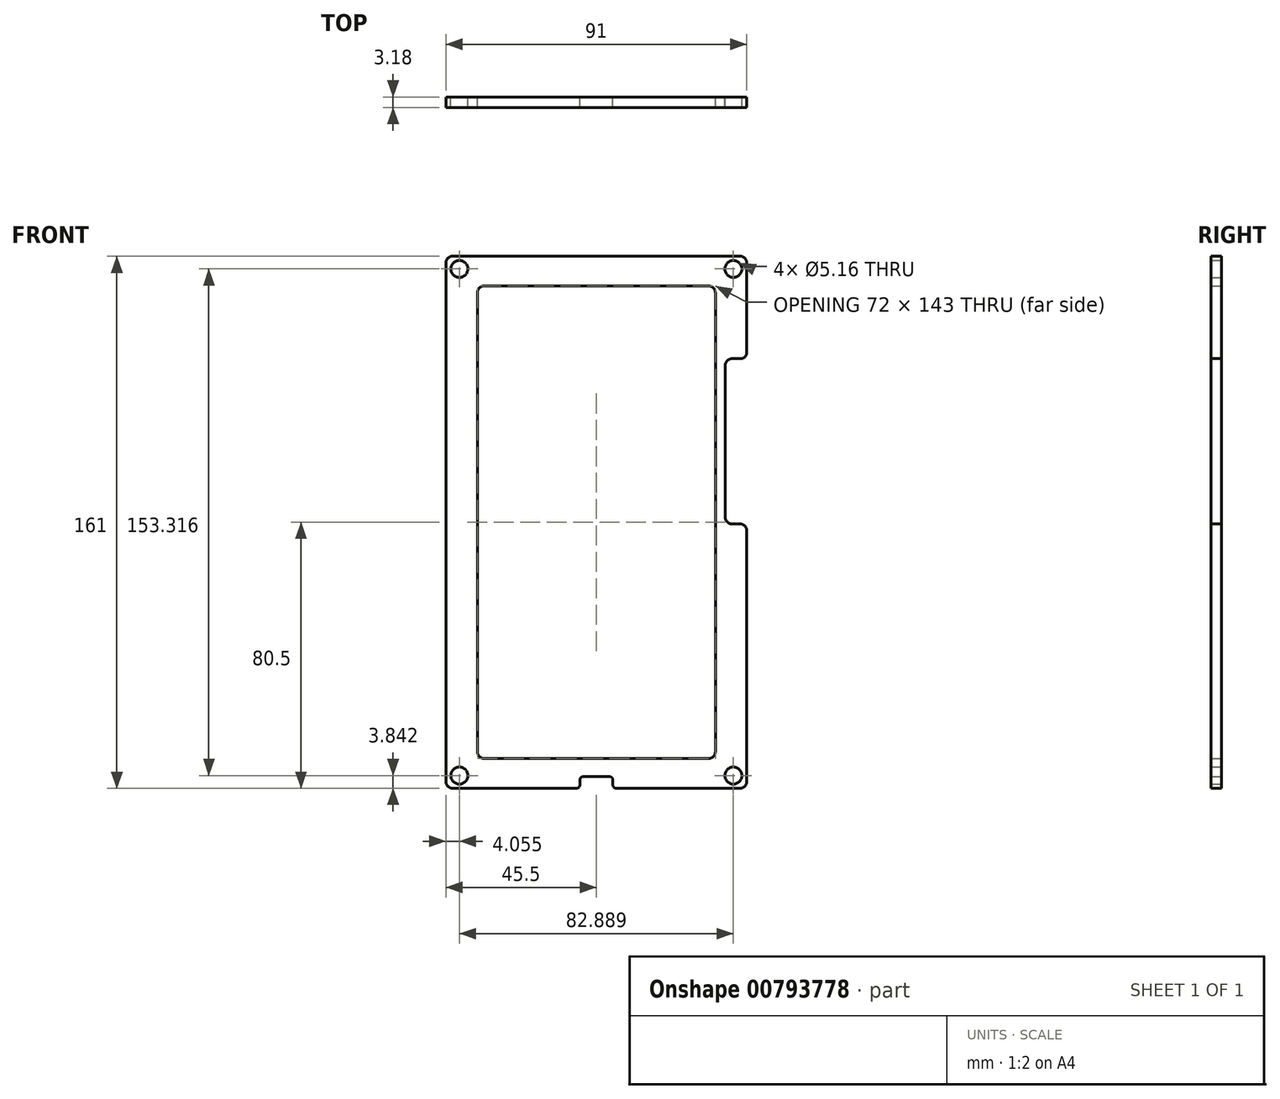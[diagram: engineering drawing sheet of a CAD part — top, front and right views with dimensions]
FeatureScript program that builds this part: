
annotation { "Feature Type Name" : "Feature", "Feature Type Description" : "" }
export const myFeature = defineFeature(function(context is Context, id is Id, definition is map)
    precondition{}
    {
        {
            var Q0;
            Q0=qCreatedBy(makeId("Front.planeOp"),FACE);
            var sketch = newSketch(context, id + "F0", { "sketchPlane" : qUnion([Q0])});
            skLineSegment(sketch, "E0.bottom", {"start": v(39, 74.5) * mm, "end": v(-39, 74.5) * mm});
            skLineSegment(sketch, "E0.top", {"start": v(39, -74.5) * mm, "end": v(-39, -74.5) * mm});
            skLineSegment(sketch, "E0.left", {"start": v(39, 74.5) * mm, "end": v(39, -74.5) * mm});
            skLineSegment(sketch, "E0.right", {"start": v(-39, 74.5) * mm, "end": v(-39, -74.5) * mm});
            skPoint(sketch, "E0.middle", {"position": v(0, 0) * mm});
            skSolve(sketch);
        }
        {
            var Q0;
            Q0=qCreatedBy(makeId("Front.planeOp"),FACE);
            var sketch = newSketch(context, id + "F1", { "sketchPlane" : qUnion([Q0])});
            skLineSegment(sketch, "E1.bottom", {"start": v(36, 71.5) * mm, "end": v(-36, 71.5) * mm});
            skLineSegment(sketch, "E1.top", {"start": v(36, -71.5) * mm, "end": v(-36, -71.5) * mm});
            skLineSegment(sketch, "E1.left", {"start": v(36, 71.5) * mm, "end": v(36, -71.5) * mm});
            skLineSegment(sketch, "E1.right", {"start": v(-36, 71.5) * mm, "end": v(-36, -71.5) * mm});
            skPoint(sketch, "E1.middle", {"position": v(0, 0) * mm});
            skLineSegment(sketch, "E2.bottom", {"start": v(45.5, 80.5) * mm, "end": v(-45.5, 80.5) * mm});
            skLineSegment(sketch, "E2.top", {"start": v(45.5, -80.5) * mm, "end": v(5, -80.5) * mm});
            skLineSegment(sketch, "E2.left", {"start": v(45.5, 80.5) * mm, "end": v(45.5, 49.5) * mm});
            skLineSegment(sketch, "E2.right", {"start": v(-45.5, 80.5) * mm, "end": v(-45.5, -80.5) * mm});
            skLineSegment(sketch, "E3", {"start": v(36, 71.5) * mm, "end": v(45.5, 80.5) * mm, "construction": true});
            skLineSegment(sketch, "E4", {"start": v(-36, 71.5) * mm, "end": v(-45.5, 80.5) * mm, "construction": true});
            skLineSegment(sketch, "E5", {"start": v(36, -71.5) * mm, "end": v(45.5, -80.5) * mm, "construction": true});
            skLineSegment(sketch, "E6", {"start": v(-36, -71.5) * mm, "end": v(-45.5, -80.5) * mm, "construction": true});
            skCircle(sketch, "E7", {"center": v(-41.44, 76.66) * mm, "radius": 2.58 * mm});
            skCircle(sketch, "E8", {"center": v(41.44, 76.66) * mm, "radius": 2.58 * mm});
            skCircle(sketch, "E9", {"center": v(41.44, -76.66) * mm, "radius": 2.58 * mm});
            skCircle(sketch, "E10", {"center": v(-41.44, -76.66) * mm, "radius": 2.58 * mm});
            skLineSegment(sketch, "E11.bottom", {"start": v(45.5, 49.5) * mm, "end": v(39, 49.5) * mm});
            skLineSegment(sketch, "E11.top", {"start": v(45.5, -0.5) * mm, "end": v(39, -0.5) * mm});
            skLineSegment(sketch, "E11.right", {"start": v(39, 49.5) * mm, "end": v(39, -0.5) * mm});
            skLineSegment(sketch, "E12.trimOffspring", {"start": v(45.5, -0.5) * mm, "end": v(45.5, -80.5) * mm});
            skLineSegment(sketch, "E13.top", {"start": v(-5, -77) * mm, "end": v(5, -77) * mm});
            skLineSegment(sketch, "E13.left", {"start": v(-5, -80.5) * mm, "end": v(-5, -77) * mm});
            skLineSegment(sketch, "E13.right", {"start": v(5, -80.5) * mm, "end": v(5, -77) * mm});
            skLineSegment(sketch, "E14", {"start": v(0, 0) * mm, "end": v(0, -100.8) * mm, "construction": true});
            skLineSegment(sketch, "E15.trimOffspring", {"start": v(-5, -80.5) * mm, "end": v(-45.5, -80.5) * mm});
            skSolve(sketch);
        }
        {
            var Q0;
            Q0=qSketchRegion(id+"F1",true);
            extrude(context, id + "F2", {"entities" : qUnion([Q0]), "depth" : 3.17 * mm, "offsetDistance" : 25 * mm});
        }
        {
            var Q0;
            Q0=makeQuery(id+"F2.opExtrude","SWEPT_EDGE",EDGE,{"disambiguationData":[OSD([sQuery(id+"F1.wireOp",EDGE,"E1.bottom"),sQuery(id+"F1.wireOp",EDGE,"E1.right")])]});
            var Q1;
            Q1=makeQuery(id+"F2.opExtrude","SWEPT_EDGE",EDGE,{"disambiguationData":[OSD([sQuery(id+"F1.wireOp",EDGE,"E1.bottom"),sQuery(id+"F1.wireOp",EDGE,"E1.left")])]});
            var Q2;
            Q2=makeQuery(id+"F2.opExtrude","SWEPT_EDGE",EDGE,{"disambiguationData":[OSD([sQuery(id+"F1.wireOp",EDGE,"E2.bottom"),sQuery(id+"F1.wireOp",EDGE,"E2.right")])]});
            var Q3;
            Q3=makeQuery(id+"F2.opExtrude","SWEPT_EDGE",EDGE,{"disambiguationData":[OSD([sQuery(id+"F1.wireOp",EDGE,"E2.bottom"),sQuery(id+"F1.wireOp",EDGE,"E2.left")])]});
            var Q4;
            Q4=makeQuery(id+"F2.opExtrude","SWEPT_EDGE",EDGE,{"disambiguationData":[OSD([sQuery(id+"F1.wireOp",EDGE,"E2.left"),sQuery(id+"F1.wireOp",EDGE,"E11.bottom")])]});
            var Q5;
            Q5=makeQuery(id+"F2.opExtrude","SWEPT_EDGE",EDGE,{"disambiguationData":[OSD([sQuery(id+"F1.wireOp",EDGE,"E11.bottom"),sQuery(id+"F1.wireOp",EDGE,"E11.right")])]});
            var Q6;
            Q6=makeQuery(id+"F2.opExtrude","SWEPT_EDGE",EDGE,{"disambiguationData":[OSD([sQuery(id+"F1.wireOp",EDGE,"E11.top"),sQuery(id+"F1.wireOp",EDGE,"E12.trimOffspring")])]});
            var Q7;
            Q7=makeQuery(id+"F2.opExtrude","SWEPT_EDGE",EDGE,{"disambiguationData":[OSD([sQuery(id+"F1.wireOp",EDGE,"E11.top"),sQuery(id+"F1.wireOp",EDGE,"E11.right")])]});
            var Q8;
            Q8=makeQuery(id+"F2.opExtrude","SWEPT_EDGE",EDGE,{"disambiguationData":[OSD([sQuery(id+"F1.wireOp",EDGE,"E1.top"),sQuery(id+"F1.wireOp",EDGE,"E1.right")])]});
            var Q9;
            Q9=makeQuery(id+"F2.opExtrude","SWEPT_EDGE",EDGE,{"disambiguationData":[OSD([sQuery(id+"F1.wireOp",EDGE,"E2.right"),sQuery(id+"F1.wireOp",EDGE,"E15.trimOffspring")])]});
            var Q10;
            Q10=makeQuery(id+"F2.opExtrude","SWEPT_EDGE",EDGE,{"disambiguationData":[OSD([sQuery(id+"F1.wireOp",EDGE,"E2.top"),sQuery(id+"F1.wireOp",EDGE,"E12.trimOffspring")])]});
            var Q11;
            Q11=makeQuery(id+"F2.opExtrude","SWEPT_EDGE",EDGE,{"disambiguationData":[OSD([sQuery(id+"F1.wireOp",EDGE,"E1.top"),sQuery(id+"F1.wireOp",EDGE,"E1.left")])]});
            fillet(context, id + "F3", {"entities" : qUnion([Q0, Q1, Q2, Q3, Q4, Q5, Q6, Q7, Q8, Q9, Q10, Q11]), "radius" : 2 * mm, "tangentPropagation" : true, "allowEdgeOverflow" : false});
        }
        {
            var Q0;
            Q0=makeQuery(id+"F2.opExtrude","SWEPT_EDGE",EDGE,{"disambiguationData":[OSD([sQuery(id+"F1.wireOp",EDGE,"E2.top"),sQuery(id+"F1.wireOp",EDGE,"E13.right")])]});
            var Q1;
            Q1=makeQuery(id+"F2.opExtrude","SWEPT_EDGE",EDGE,{"disambiguationData":[OSD([sQuery(id+"F1.wireOp",EDGE,"E13.top"),sQuery(id+"F1.wireOp",EDGE,"E13.right")])]});
            var Q2;
            Q2=makeQuery(id+"F2.opExtrude","SWEPT_EDGE",EDGE,{"disambiguationData":[OSD([sQuery(id+"F1.wireOp",EDGE,"E13.top"),sQuery(id+"F1.wireOp",EDGE,"E13.left")])]});
            var Q3;
            Q3=makeQuery(id+"F2.opExtrude","SWEPT_EDGE",EDGE,{"disambiguationData":[OSD([sQuery(id+"F1.wireOp",EDGE,"E13.left"),sQuery(id+"F1.wireOp",EDGE,"E15.trimOffspring")])]});
            fillet(context, id + "F4", {"entities" : qUnion([Q0, Q1, Q2, Q3]), "radius" : 1 * mm, "tangentPropagation" : true, "allowEdgeOverflow" : false});
        }
    });
